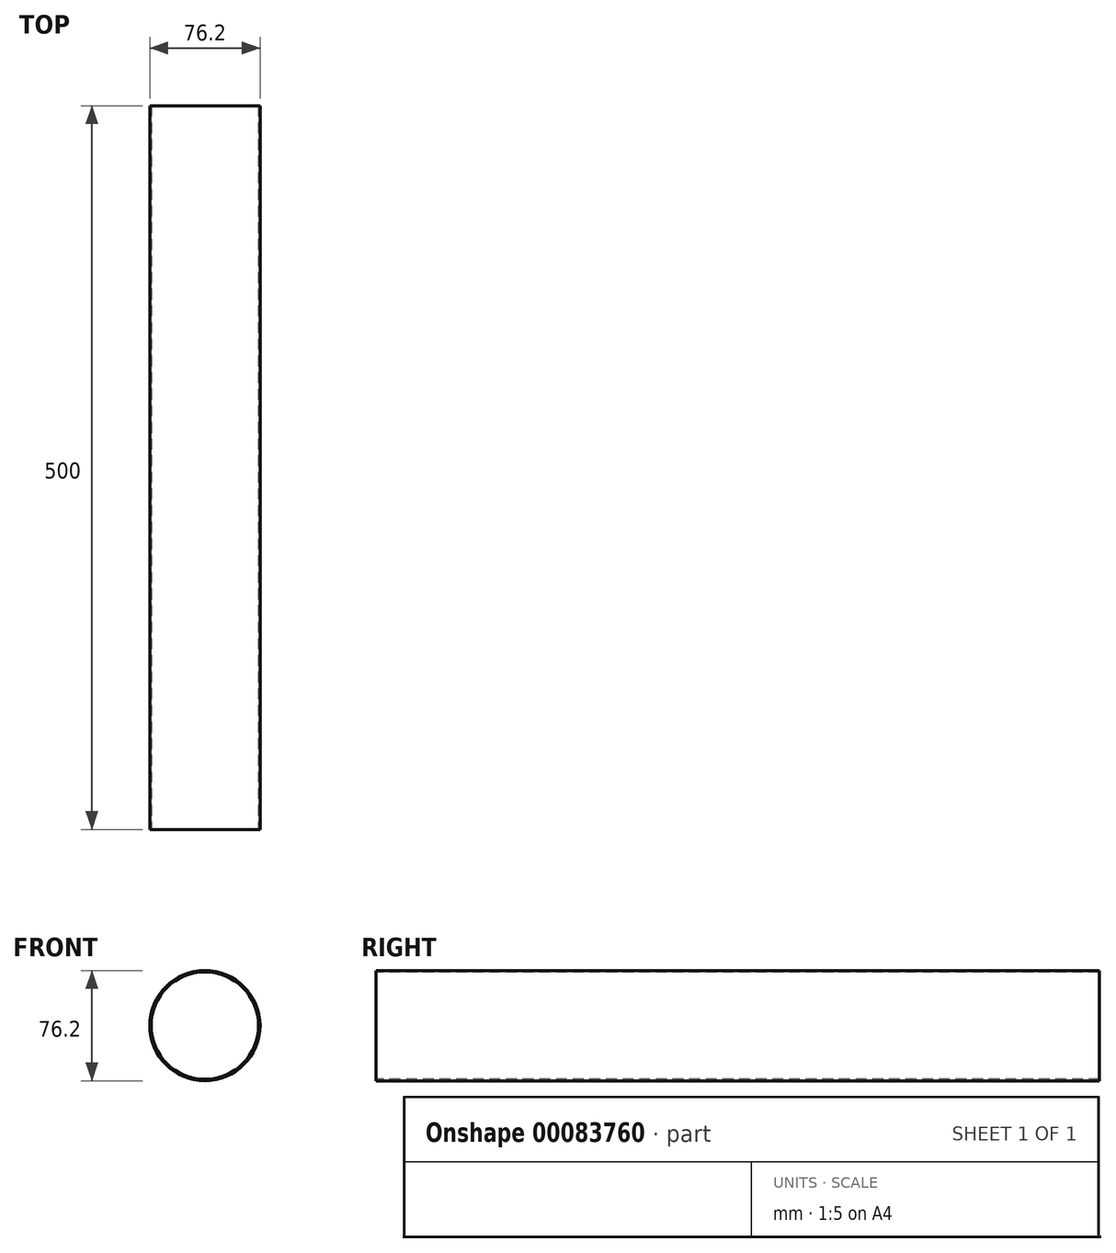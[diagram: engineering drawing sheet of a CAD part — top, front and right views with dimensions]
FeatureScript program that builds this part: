
annotation { "Feature Type Name" : "Feature", "Feature Type Description" : "" }
export const myFeature = defineFeature(function(context is Context, id is Id, definition is map)
    precondition{}
    {
        {
            var Q0;
            Q0=qCreatedBy(makeId("Front.planeOp"),FACE);
            var sketch = newSketch(context, id + "F0", { "sketchPlane" : qUnion([Q0])});
            skCircle(sketch, "E0", {"center": v(0, 0) * mm, "radius": 38.1 * mm});
            skCircle(sketch, "E1", {"center": v(0, 0) * mm, "radius": 37.1 * mm});
            skSolve(sketch);
        }
        {
            var Q0;
            Q0=sQuery(id+"F0.wireOp",EDGE,"E0");
            var Q1;
            Q1=sQuery(id+"F0.wireOp",EDGE,"E1");
            extrude(context, id + "F1", {"bodyType" : ToolBodyType.SURFACE, "surfaceEntities" : qUnion([Q0, Q1]), "depth" : 500 * mm});
        }
    });
